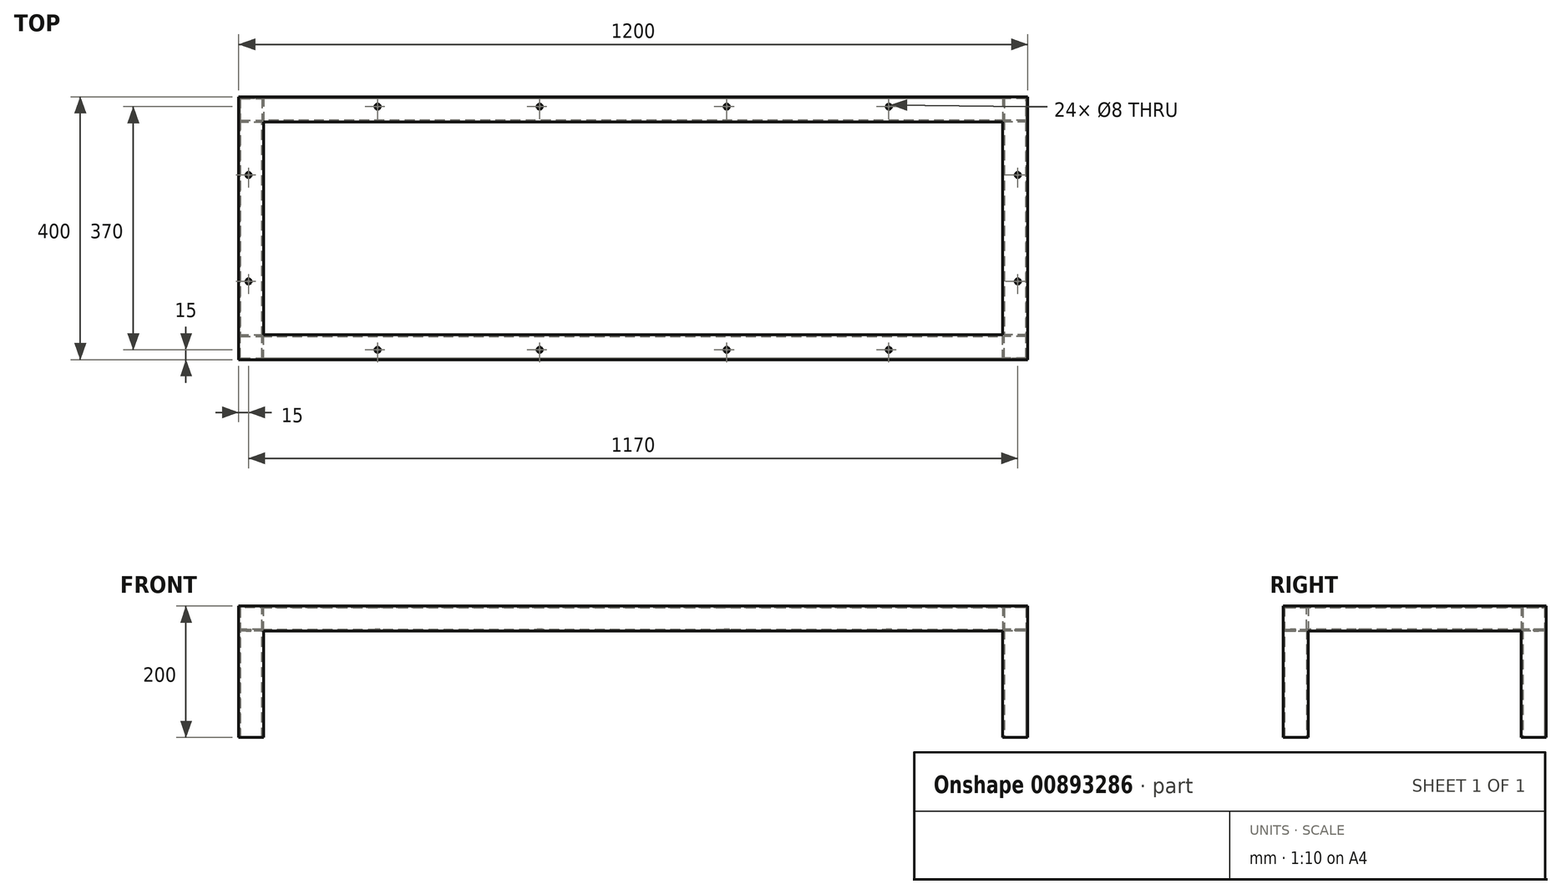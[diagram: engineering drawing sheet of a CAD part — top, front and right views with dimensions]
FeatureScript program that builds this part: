
annotation { "Feature Type Name" : "Feature", "Feature Type Description" : "" }
export const myFeature = defineFeature(function(context is Context, id is Id, definition is map)
    precondition{}
    {
        {
            var Q0;
            Q0=qCreatedBy(makeId("Front.planeOp"),FACE);
            var sketch = newSketch(context, id + "F0", { "sketchPlane" : qUnion([Q0])});
            skLineSegment(sketch, "E0.bottom", {"start": v(0, 0) * mm, "end": v(38, 0) * mm});
            skLineSegment(sketch, "E0.top", {"start": v(0, 200) * mm, "end": v(38, 200) * mm});
            skLineSegment(sketch, "E0.left", {"start": v(0, 0) * mm, "end": v(0, 200) * mm});
            skLineSegment(sketch, "E0.right", {"start": v(38, 0) * mm, "end": v(38, 162) * mm});
            skLineSegment(sketch, "E1.bottom", {"start": v(38, 200) * mm, "end": v(1200, 200) * mm});
            skLineSegment(sketch, "E1.top", {"start": v(38, 162) * mm, "end": v(1162, 162) * mm});
            skLineSegment(sketch, "E2.bottom", {"start": v(1200, 200) * mm, "end": v(1162, 200) * mm});
            skLineSegment(sketch, "E2.top", {"start": v(1200, 0) * mm, "end": v(1162, 0) * mm});
            skLineSegment(sketch, "E2.left", {"start": v(1200, 200) * mm, "end": v(1200, 0) * mm});
            skLineSegment(sketch, "E2.right", {"start": v(1162, 162) * mm, "end": v(1162, 0) * mm});
            skSolve(sketch);
        }
        {
            var Q0;
            Q0=qSketchRegion(id+"F0",true);
            extrude(context, id + "F1", {"entities" : qUnion([Q0]), "depth" : 38 * mm, "offsetDistance" : 25 * mm});
        }
        {
            var Q0;
            Q0=makeQuery(id+"F1.opExtrude","SWEPT_FACE",FACE,{"disambiguationData":[OSD([sQuery(id+"F0.wireOp",EDGE,"E0.left")])]});
            var sketch = newSketch(context, id + "F2", { "sketchPlane" : qUnion([Q0])});
            skLineSegment(sketch, "E3", {"start": v(0, 200) * mm, "end": v(-324, 200) * mm});
            skLineSegment(sketch, "E4", {"start": v(-324, 200) * mm, "end": v(-324, 162) * mm});
            skLineSegment(sketch, "E5", {"start": v(-324, 162) * mm, "end": v(0, 162) * mm});
            skSolve(sketch);
        }
        {
            var Q0;
            Q0=qSketchRegion(id+"F2",true);
            var Q1;
            {var subQ0=sQuery(id+"F2.wireOp",EDGE,"E3");Q1=makeQuery(id+"F2.imprint","IMPRINT",FACE,{"disambiguationData":[TD([[makeQuery(id+"F2.imprint","IMPRINT",EDGE,{"derivedFrom":subQ0}),1.0]])]});}
            extrude(context, id + "F3", {"entities" : qUnion([Q0, Q1]), "operationType" : NewBodyOperationType.ADD, "oppositeDirection" : true, "depth" : 38 * mm, "offsetDistance" : 25 * mm});
        }
        {
            var Q0;
            {var subQ0=sQuery(id+"F0.wireOp",EDGE,"E0.right");var subQ2=sQuery(id+"F0.wireOp",EDGE,"E2.bottom");var subQ3=sQuery(id+"F0.wireOp",EDGE,"E1.bottom");var subQ4=sQuery(id+"F0.wireOp",EDGE,"E0.top");var subQ6=sQuery(id+"F0.wireOp",EDGE,"E0.left");var subQ7=sQuery(id+"F0.wireOp",EDGE,"E1.top");var subQ8=sQuery(id+"F0.wireOp",EDGE,"E2.right");var subQ9=sQuery(id+"F0.wireOp",EDGE,"E2.left");var subQ10=sQuery(id+"F0.wireOp",EDGE,"E2.top");var subQ11=makeQuery(id+"F1.opExtrude","CAP_FACE",FACE,{"disambiguationData":[OSD([sQuery(id+"F0.wireOp",EDGE,"E0.bottom"),subQ4,subQ6,subQ0,subQ3,subQ7,subQ2,subQ10,subQ9,subQ8])],"isStart":true});Q0=makeQuery(id+"F3.boolean.opBoolean","SPLIT",FACE,{"disambiguationData":[TD([makeQuery(id+"F1.opExtrude","SWEPT_FACE",FACE,{"disambiguationData":[OSD([subQ10])]})])],"derivedFrom":subQ11});}
            var sketch = newSketch(context, id + "F4", { "sketchPlane" : qUnion([Q0])});
            skLineSegment(sketch, "E6.bottom", {"start": v(-1200, 200) * mm, "end": v(-1162, 200) * mm});
            skLineSegment(sketch, "E6.top", {"start": v(-1200, 162) * mm, "end": v(-1162, 162) * mm});
            skLineSegment(sketch, "E6.left", {"start": v(-1200, 200) * mm, "end": v(-1200, 162) * mm});
            skLineSegment(sketch, "E6.right", {"start": v(-1162, 200) * mm, "end": v(-1162, 162) * mm});
            skSolve(sketch);
        }
        {
            var Q0;
            Q0=qSketchRegion(id+"F4",true);
            extrude(context, id + "F5", {"entities" : qUnion([Q0]), "operationType" : NewBodyOperationType.ADD, "depth" : 324 * mm, "offsetDistance" : 25 * mm});
        }
        {
            var Q0;
            Q0=makeQuery(id+"F5.opExtrude","CAP_FACE",FACE,{"disambiguationData":[OSD([sQuery(id+"F4.wireOp",EDGE,"E6.bottom"),sQuery(id+"F4.wireOp",EDGE,"E6.top"),sQuery(id+"F4.wireOp",EDGE,"E6.left"),sQuery(id+"F4.wireOp",EDGE,"E6.right")])],"isStart":false});
            var sketch = newSketch(context, id + "F6", { "sketchPlane" : qUnion([Q0])});
            skLineSegment(sketch, "E7.bottom", {"start": v(-1200, 200) * mm, "end": v(0, 200) * mm});
            skLineSegment(sketch, "E7.top", {"start": v(-1162, 162) * mm, "end": v(-38, 162) * mm});
            skLineSegment(sketch, "E7.left", {"start": v(-1200, 200) * mm, "end": v(-1200, 162) * mm});
            skLineSegment(sketch, "E7.right", {"start": v(0, 200) * mm, "end": v(0, 162) * mm});
            skLineSegment(sketch, "E8.bottom", {"start": v(-1200, 200) * mm, "end": v(-1162, 200) * mm});
            skLineSegment(sketch, "E8.top", {"start": v(-1200, 0) * mm, "end": v(-1162, 0) * mm});
            skLineSegment(sketch, "E8.left", {"start": v(-1200, 200) * mm, "end": v(-1200, 0) * mm});
            skLineSegment(sketch, "E8.right", {"start": v(-1162, 162) * mm, "end": v(-1162, 0) * mm});
            skLineSegment(sketch, "E9.bottom", {"start": v(0, 200) * mm, "end": v(-38, 200) * mm});
            skLineSegment(sketch, "E9.top", {"start": v(0, 0) * mm, "end": v(-38, 0) * mm});
            skLineSegment(sketch, "E9.left", {"start": v(0, 200) * mm, "end": v(0, 0) * mm});
            skLineSegment(sketch, "E9.right", {"start": v(-38, 162) * mm, "end": v(-38, 0) * mm});
            skSolve(sketch);
        }
        {
            var Q0;
            Q0=qSketchRegion(id+"F6",true);
            extrude(context, id + "F7", {"entities" : qUnion([Q0]), "operationType" : NewBodyOperationType.ADD, "depth" : 38 * mm, "offsetDistance" : 25 * mm});
        }
        {
            var Q0;
            Q0=makeQuery(id+"F7.opExtrude","SWEPT_FACE",FACE,{"disambiguationData":[OSD([sQuery(id+"F6.wireOp",EDGE,"E9.top")])]});
            var Q1;
            Q1=makeQuery(id+"F1.opExtrude","SWEPT_FACE",FACE,{"disambiguationData":[OSD([sQuery(id+"F0.wireOp",EDGE,"E0.bottom")])]});
            var Q2;
            Q2=makeQuery(id+"F1.opExtrude","SWEPT_FACE",FACE,{"disambiguationData":[OSD([sQuery(id+"F0.wireOp",EDGE,"E2.top")])]});
            var Q3;
            Q3=makeQuery(id+"F7.opExtrude","SWEPT_FACE",FACE,{"disambiguationData":[OSD([sQuery(id+"F6.wireOp",EDGE,"E8.top")])]});
            shell(context, id + "F8", {"entities" : qUnion([Q0, Q1, Q2, Q3]), "thickness" : 2.5 * mm});
        }
        {
            var Q0;
            Q0=makeQuery(id+"F7.boolean.opBoolean","MERGE",FACE,{"derivedFrom":[makeQuery(id+"F5.boolean.opBoolean","MERGE",FACE,{"derivedFrom":[makeQuery(id+"F3.boolean.opBoolean","MERGE",FACE,{"derivedFrom":[makeQuery(id+"F1.opExtrude","SWEPT_FACE",FACE,{"disambiguationData":[OSD([sQuery(id+"F0.wireOp",EDGE,"E0.top"),sQuery(id+"F0.wireOp",EDGE,"E1.bottom"),sQuery(id+"F0.wireOp",EDGE,"E2.bottom")])]}),makeQuery(id+"F3.opExtrude","SWEPT_FACE",FACE,{"disambiguationData":[OSD([sQuery(id+"F2.wireOp",EDGE,"E3")])]})]}),makeQuery(id+"F5.opExtrude","SWEPT_FACE",FACE,{"disambiguationData":[OSD([sQuery(id+"F4.wireOp",EDGE,"E6.bottom")])]})]}),makeQuery(id+"F7.opExtrude","SWEPT_FACE",FACE,{"disambiguationData":[OSD([sQuery(id+"F6.wireOp",EDGE,"E7.bottom"),sQuery(id+"F6.wireOp",EDGE,"E8.bottom"),sQuery(id+"F6.wireOp",EDGE,"E9.bottom")])]})]});
            var sketch = newSketch(context, id + "F9", { "sketchPlane" : qUnion([Q0])});
            skLineSegment(sketch, "E10", {"start": v(211.25, 362) * mm, "end": v(211.25, 347) * mm});
            skCircle(sketch, "E11", {"center": v(211.25, 347) * mm, "radius": 4 * mm});
            skLineSegment(sketch, "E12", {"start": v(211.25, 347) * mm, "end": v(457.75, 347) * mm});
            skCircle(sketch, "E13", {"center": v(457.75, 347) * mm, "radius": 4 * mm});
            skLineSegment(sketch, "E14", {"start": v(600, 362) * mm, "end": v(600, -38) * mm, "construction": true});
            skLineSegment(sketch, "E15", {"start": v(0, 162) * mm, "end": v(1200, 162) * mm, "construction": true});
            skCircle(sketch, "E16.MirrorC", {"center": v(988.75, 347) * mm, "radius": 4 * mm});
            skCircle(sketch, "E17.MirrorC", {"center": v(742.25, 347) * mm, "radius": 4 * mm});
            skCircle(sketch, "E18.MirrorC", {"center": v(211.25, -23) * mm, "radius": 4 * mm});
            skCircle(sketch, "E19.MirrorC", {"center": v(457.75, -23) * mm, "radius": 4 * mm});
            skCircle(sketch, "E20.MirrorC", {"center": v(742.25, -23) * mm, "radius": 4 * mm});
            skCircle(sketch, "E21.MirrorC", {"center": v(988.75, -23) * mm, "radius": 4 * mm});
            skLineSegment(sketch, "E22", {"start": v(0, 0) * mm, "end": v(38, 0) * mm});
            skLineSegment(sketch, "E23", {"start": v(0, 0) * mm, "end": v(0, 81) * mm});
            skLineSegment(sketch, "E24", {"start": v(0, 81) * mm, "end": v(15, 81) * mm});
            skCircle(sketch, "E25", {"center": v(15, 81) * mm, "radius": 4 * mm});
            skCircle(sketch, "E26.MirrorC", {"center": v(15, 243) * mm, "radius": 4 * mm});
            skCircle(sketch, "E27.MirrorC", {"center": v(1185, 243) * mm, "radius": 4 * mm});
            skCircle(sketch, "E28.MirrorC", {"center": v(1185, 81) * mm, "radius": 4 * mm});
            skLineSegment(sketch, "E29", {"start": v(38, 0) * mm, "end": v(38, -38) * mm});
            skSolve(sketch);
        }
        {
            var Q0;
            Q0 = qSketchRegion(id + "F9", true);
            extrude(context, id + "F10", {"entities" : qUnion([Q0]), "operationType" : NewBodyOperationType.REMOVE, "endBound" : BoundingType.THROUGH_ALL, "oppositeDirection" : true, "depth" : 25 * mm, "offsetDistance" : 25 * mm});
        }
    });
